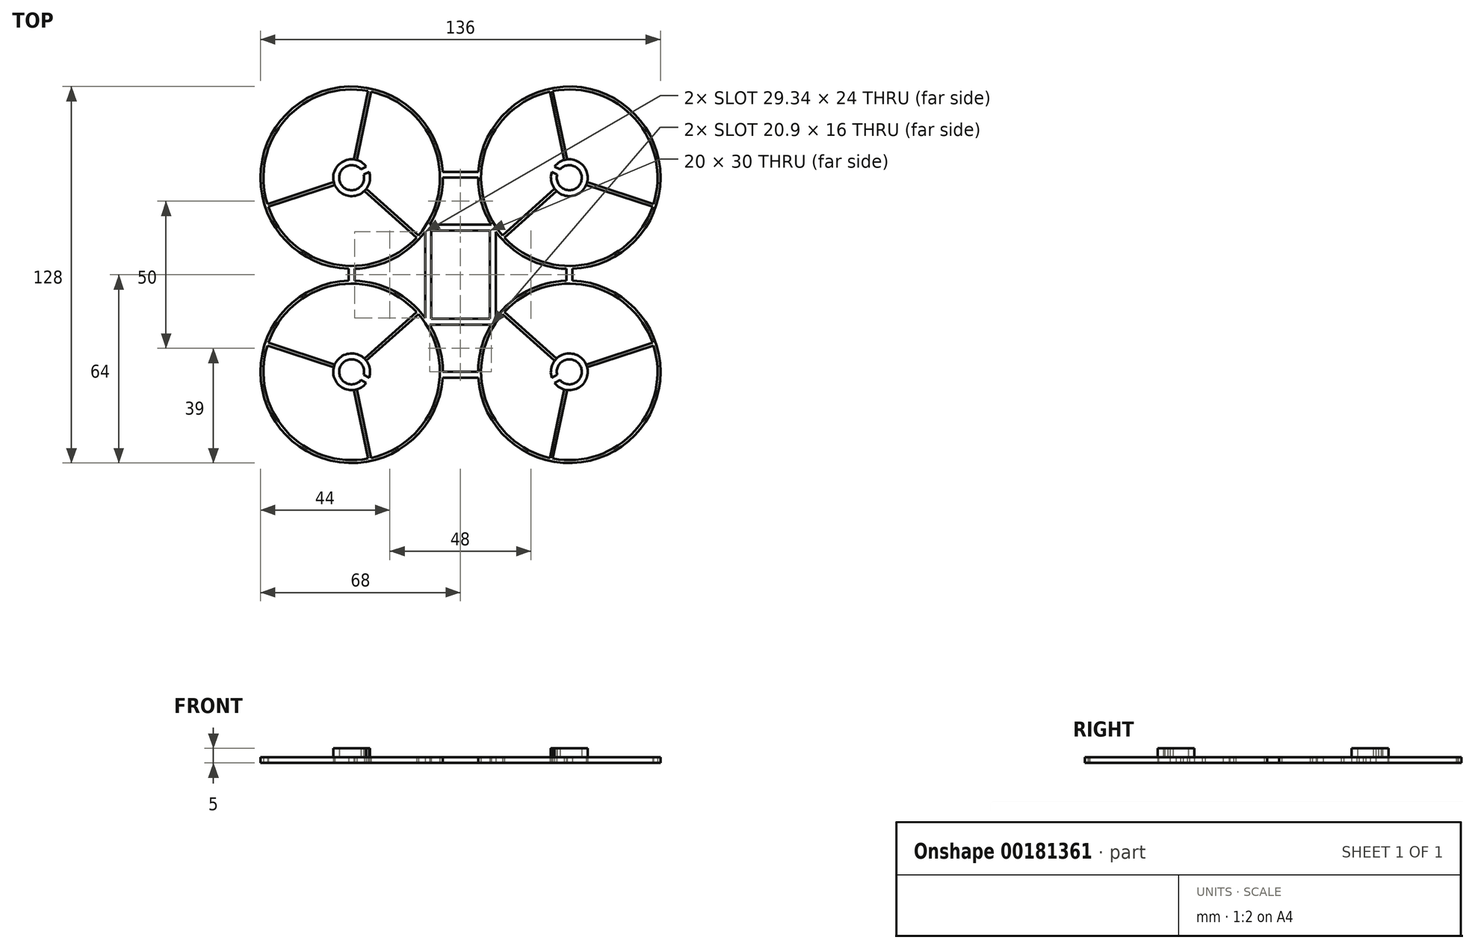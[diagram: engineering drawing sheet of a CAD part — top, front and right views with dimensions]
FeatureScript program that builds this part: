
annotation { "Feature Type Name" : "Feature", "Feature Type Description" : "" }
export const myFeature = defineFeature(function(context is Context, id is Id, definition is map)
    precondition{}
    {
        {
            var Q0;
            Q0=qCreatedBy(makeId("Top.planeOp"),FACE);
            var sketch = newSketch(context, id + "F0", { "sketchPlane" : qUnion([Q0])});
            skLineSegment(sketch, "E0.bottom", {"start": v(10, -15) * mm, "end": v(-10, -15) * mm});
            skLineSegment(sketch, "E0.left", {"start": v(10, -15) * mm, "end": v(10, 15) * mm});
            skPoint(sketch, "E0.middle", {"position": v(0, 0) * mm});
            skLineSegment(sketch, "E1.trimOffspring", {"start": v(-10, -15) * mm, "end": v(-10, 15) * mm});
            skPoint(sketch, "E0.right.start.orphan", {"position": v(-10, -15) * mm});
            skPoint(sketch, "E2.orphan", {"position": v(10, -15) * mm});
            skLineSegment(sketch, "E3.trimOffspring", {"start": v(10, 15) * mm, "end": v(-10, 15) * mm});
            skPoint(sketch, "E0.top.start.orphan", {"position": v(10, 15) * mm});
            skPoint(sketch, "E4.trimOffspring.end.orphan", {"position": v(-10, 15) * mm});
            skLineSegment(sketch, "E5", {"start": v(0, 0) * mm, "end": v(-37, 0) * mm});
            skCircle(sketch, "E6", {"center": v(-37, 33) * mm, "radius": 30 * mm});
            skCircle(sketch, "E7", {"center": v(-37, -33) * mm, "radius": 30 * mm});
            skArc(sketch, "E8", {"start": v(-10.45, 17) * mm, "mid": v(-7.13, 24.7) * mm, "end": v(-6, 33) * mm});
            skArc(sketch, "E9", {"start": v(-12, -14.67) * mm, "mid": v(-22.54, -5.58) * mm, "end": v(-36, -2.02) * mm});
            skLineSegment(sketch, "E10.0", {"start": v(-12, -14.67) * mm, "end": v(-12, 14.67) * mm});
            skLineSegment(sketch, "E11.0", {"start": v(10.45, 17) * mm, "end": v(-10.45, 17) * mm});
            skLineSegment(sketch, "E12.0", {"start": v(12, -14.67) * mm, "end": v(12, 14.67) * mm});
            skLineSegment(sketch, "E13.0", {"start": v(10.45, -17) * mm, "end": v(-10.45, -17) * mm});
            skCircle(sketch, "E14.MirrorC", {"center": v(37, -33) * mm, "radius": 30 * mm});
            skArc(sketch, "E15.MirrorC", {"start": v(10.45, 17) * mm, "mid": v(7.13, 24.7) * mm, "end": v(6, 33) * mm});
            skCircle(sketch, "E16.MirrorC", {"center": v(37, 33) * mm, "radius": 30 * mm});
            skArc(sketch, "E17.MirrorC", {"start": v(12, -14.67) * mm, "mid": v(22.54, -5.58) * mm, "end": v(36, -2.02) * mm});
            skLineSegment(sketch, "E18.0", {"start": v(-36, -2.02) * mm, "end": v(-36, 2.02) * mm});
            skLineSegment(sketch, "E19.0", {"start": v(-38, -2.02) * mm, "end": v(-38, 2.02) * mm});
            skArc(sketch, "E20.trimOffspring", {"start": v(-36, 2.02) * mm, "mid": v(-22.54, 5.58) * mm, "end": v(-12, 14.67) * mm});
            skArc(sketch, "E21.trimOffspring", {"start": v(-38, -2.02) * mm, "mid": v(-59.27, -54.56) * mm, "end": v(-6.06, -35) * mm});
            skLineSegment(sketch, "E22", {"start": v(-6, 33) * mm, "end": v(6, 33) * mm});
            skLineSegment(sketch, "E23", {"start": v(-6, -33) * mm, "end": v(6, -33) * mm});
            skLineSegment(sketch, "E24.0", {"start": v(-6.06, 35) * mm, "end": v(6.06, 35) * mm});
            skLineSegment(sketch, "E25.0", {"start": v(-6.06, -35) * mm, "end": v(6.06, -35) * mm});
            skArc(sketch, "E26.trimOffspring", {"start": v(-6.06, 35) * mm, "mid": v(-59.27, 54.56) * mm, "end": v(-38, 2.02) * mm});
            skArc(sketch, "E27.trimOffspring", {"start": v(6.06, 35) * mm, "mid": v(59.27, 54.56) * mm, "end": v(38, 2.02) * mm});
            skArc(sketch, "E28.trimOffspring", {"start": v(-6, -33) * mm, "mid": v(-7.13, -24.7) * mm, "end": v(-10.45, -17) * mm});
            skArc(sketch, "E29.trimOffspring", {"start": v(6, -33) * mm, "mid": v(7.13, -24.7) * mm, "end": v(10.45, -17) * mm});
            skLineSegment(sketch, "E30.MirrorCS", {"start": v(36, -2.02) * mm, "end": v(36, 2.02) * mm});
            skLineSegment(sketch, "E31.MirrorCS", {"start": v(38, -2.02) * mm, "end": v(38, 2.02) * mm});
            skArc(sketch, "E32.trimOffspring", {"start": v(36, 2.02) * mm, "mid": v(22.54, 5.58) * mm, "end": v(12, 14.67) * mm});
            skArc(sketch, "E33.trimOffspring", {"start": v(38, -2.02) * mm, "mid": v(59.27, -54.56) * mm, "end": v(6.06, -35) * mm});
            skSolve(sketch);
        }
        {
            var Q0;
            Q0=makeQuery(id+"F0.imprint","IMPRINT",FACE,{"disambiguationData":[TD([[makeQuery(id+"F0.imprint","IMPRINT",EDGE,{"derivedFrom":sQuery(id+"F0.wireOp",EDGE,"E0.bottom")}),1.0]])]});
            extrude(context, id + "F1", {"entities" : qUnion([Q0]), "depth" : 2 * mm});
        }
        {
            var Q0;
            Q0=qCreatedBy(makeId("Top.planeOp"),FACE);
            var sketch = newSketch(context, id + "F2", { "sketchPlane" : qUnion([Q0])});
            skPoint(sketch, "E34.0", {"position": v(-37, 33) * mm});
            skPoint(sketch, "E34.1", {"position": v(-37, -33) * mm});
            skPoint(sketch, "E34.2", {"position": v(37, -33) * mm});
            skPoint(sketch, "E34.3", {"position": v(37, 33) * mm});
            skArc(sketch, "E35", {"start": v(-33.81, 35.81) * mm, "mid": v(-40.76, 31.02) * mm, "end": v(-32.88, 34.04) * mm});
            skArc(sketch, "E36", {"start": v(-32.01, 36.76) * mm, "mid": v(-42.53, 30.08) * mm, "end": v(-31.08, 35) * mm});
            skArc(sketch, "E37.0", {"start": v(-30.41, 62.27) * mm, "mid": v(-30.9, 62.37) * mm, "end": v(-31.4, 62.47) * mm});
            skLineSegment(sketch, "E38.0", {"start": v(-37.16, 33.47) * mm, "end": v(-37.43, 33.38) * mm});
            skLineSegment(sketch, "E39.0", {"start": v(-36.84, 32.53) * mm, "end": v(-37.12, 32.43) * mm});
            skLineSegment(sketch, "E40.0", {"start": v(-36.51, 32.9) * mm, "end": v(-36.45, 33.18) * mm});
            skLineSegment(sketch, "E41.0", {"start": v(-37.49, 33.1) * mm, "end": v(-37.43, 33.38) * mm});
            skLineSegment(sketch, "E42.0", {"start": v(-37.33, 32.63) * mm, "end": v(-37.12, 32.43) * mm});
            skLineSegment(sketch, "E43.0", {"start": v(-36.67, 33.37) * mm, "end": v(-36.45, 33.18) * mm});
            skLineSegment(sketch, "E44.trimOffspring", {"start": v(-35.24, 39) * mm, "end": v(-30.41, 62.27) * mm});
            skLineSegment(sketch, "E45.trimOffspring", {"start": v(-36.22, 39.2) * mm, "end": v(-31.4, 62.48) * mm});
            skLineSegment(sketch, "E46.trimOffspring", {"start": v(-32.02, 29.23) * mm, "end": v(-14.28, 13.4) * mm});
            skLineSegment(sketch, "E47.trimOffspring", {"start": v(-32.68, 28.48) * mm, "end": v(-14.95, 12.66) * mm});
            skLineSegment(sketch, "E48.trimOffspring", {"start": v(-42.76, 30.57) * mm, "end": v(-65.33, 23.12) * mm});
            skLineSegment(sketch, "E49.trimOffspring", {"start": v(-43.07, 31.52) * mm, "end": v(-65.64, 24.07) * mm});
            skArc(sketch, "E50.trimOffspring", {"start": v(-14.95, 12.66) * mm, "mid": v(-14.61, 13.03) * mm, "end": v(-14.28, 13.4) * mm});
            skArc(sketch, "E51.trimOffspring", {"start": v(-65.64, 24.07) * mm, "mid": v(-65.49, 23.6) * mm, "end": v(-65.33, 23.12) * mm});
            skLineSegment(sketch, "E52", {"start": v(-37, 33) * mm, "end": v(-36.53, 33.25) * mm});
            skLineSegment(sketch, "E53.0", {"start": v(-32.88, 34.04) * mm, "end": v(-31.08, 35) * mm});
            skLineSegment(sketch, "E54.0", {"start": v(-33.81, 35.81) * mm, "end": v(-32.01, 36.76) * mm});
            skLineSegment(sketch, "E55.MirrorCS", {"start": v(37.16, 33.47) * mm, "end": v(37.43, 33.38) * mm});
            skLineSegment(sketch, "E56.MirrorCS", {"start": v(36.84, 32.53) * mm, "end": v(37.12, 32.43) * mm});
            skLineSegment(sketch, "E57.MirrorCS", {"start": v(37, 33) * mm, "end": v(36.53, 33.25) * mm});
            skLineSegment(sketch, "E58.MirrorCS", {"start": v(37.49, 33.1) * mm, "end": v(37.43, 33.38) * mm});
            skLineSegment(sketch, "E59.MirrorCS", {"start": v(37.33, 32.63) * mm, "end": v(37.12, 32.43) * mm});
            skLineSegment(sketch, "E60.MirrorCS", {"start": v(36.67, 33.37) * mm, "end": v(36.45, 33.18) * mm});
            skLineSegment(sketch, "E61.MirrorCS", {"start": v(36.51, 32.9) * mm, "end": v(36.45, 33.18) * mm});
            skLineSegment(sketch, "E62.MirrorCS", {"start": v(32.88, 34.04) * mm, "end": v(31.08, 35) * mm});
            skArc(sketch, "E63.MirrorCS", {"start": v(30.41, 62.27) * mm, "mid": v(30.9, 62.37) * mm, "end": v(31.4, 62.47) * mm});
            skArc(sketch, "E64.MirrorCS", {"start": v(65.64, 24.07) * mm, "mid": v(65.49, 23.6) * mm, "end": v(65.33, 23.12) * mm});
            skArc(sketch, "E65.MirrorCS", {"start": v(14.95, 12.66) * mm, "mid": v(14.61, 13.03) * mm, "end": v(14.28, 13.4) * mm});
            skLineSegment(sketch, "E66.MirrorCS", {"start": v(33.81, 35.81) * mm, "end": v(32.01, 36.76) * mm});
            skArc(sketch, "E67.MirrorCS", {"start": v(32.01, 36.76) * mm, "mid": v(42.53, 30.08) * mm, "end": v(31.08, 35) * mm});
            skLineSegment(sketch, "E68.MirrorCS", {"start": v(32.68, 28.48) * mm, "end": v(14.95, 12.66) * mm});
            skLineSegment(sketch, "E69.MirrorCS", {"start": v(32.02, 29.23) * mm, "end": v(14.28, 13.4) * mm});
            skLineSegment(sketch, "E70.MirrorCS", {"start": v(43.07, 31.52) * mm, "end": v(65.64, 24.07) * mm});
            skLineSegment(sketch, "E71.MirrorCS", {"start": v(35.24, 39) * mm, "end": v(30.41, 62.27) * mm});
            skLineSegment(sketch, "E72.MirrorCS", {"start": v(42.76, 30.57) * mm, "end": v(65.33, 23.12) * mm});
            skLineSegment(sketch, "E73.MirrorCS", {"start": v(36.22, 39.2) * mm, "end": v(31.4, 62.48) * mm});
            skArc(sketch, "E74.MirrorCS", {"start": v(33.81, 35.81) * mm, "mid": v(40.76, 31.02) * mm, "end": v(32.88, 34.04) * mm});
            skLineSegment(sketch, "E75.MirrorCS", {"start": v(-37, -33) * mm, "end": v(-36.53, -33.25) * mm});
            skLineSegment(sketch, "E76.MirrorCS", {"start": v(-36.84, -32.53) * mm, "end": v(-37.12, -32.43) * mm});
            skLineSegment(sketch, "E77.MirrorCS", {"start": v(-37.16, -33.47) * mm, "end": v(-37.43, -33.38) * mm});
            skLineSegment(sketch, "E78.MirrorCS", {"start": v(-37.33, -32.63) * mm, "end": v(-37.12, -32.43) * mm});
            skLineSegment(sketch, "E79.MirrorCS", {"start": v(-36.67, -33.37) * mm, "end": v(-36.45, -33.18) * mm});
            skLineSegment(sketch, "E80.MirrorCS", {"start": v(-36.51, -32.9) * mm, "end": v(-36.45, -33.18) * mm});
            skLineSegment(sketch, "E81.MirrorCS", {"start": v(36.67, -33.37) * mm, "end": v(36.45, -33.18) * mm});
            skLineSegment(sketch, "E82.MirrorCS", {"start": v(-37.49, -33.1) * mm, "end": v(-37.43, -33.38) * mm});
            skLineSegment(sketch, "E83.MirrorCS", {"start": v(37.49, -33.1) * mm, "end": v(37.43, -33.38) * mm});
            skLineSegment(sketch, "E84.MirrorCS", {"start": v(37.33, -32.63) * mm, "end": v(37.12, -32.43) * mm});
            skLineSegment(sketch, "E85.MirrorCS", {"start": v(37.16, -33.47) * mm, "end": v(37.43, -33.38) * mm});
            skLineSegment(sketch, "E86.MirrorCS", {"start": v(36.84, -32.53) * mm, "end": v(37.12, -32.43) * mm});
            skLineSegment(sketch, "E87.MirrorCS", {"start": v(37, -33) * mm, "end": v(36.53, -33.25) * mm});
            skLineSegment(sketch, "E88.MirrorCS", {"start": v(36.51, -32.9) * mm, "end": v(36.45, -33.18) * mm});
            skLineSegment(sketch, "E89.MirrorCS", {"start": v(-32.88, -34.04) * mm, "end": v(-31.08, -35) * mm});
            skArc(sketch, "E90.MirrorCS", {"start": v(14.95, -12.66) * mm, "mid": v(14.61, -13.03) * mm, "end": v(14.28, -13.4) * mm});
            skArc(sketch, "E91.MirrorCS", {"start": v(30.41, -62.27) * mm, "mid": v(30.9, -62.37) * mm, "end": v(31.4, -62.47) * mm});
            skArc(sketch, "E92.MirrorCS", {"start": v(65.64, -24.07) * mm, "mid": v(65.49, -23.6) * mm, "end": v(65.33, -23.12) * mm});
            skArc(sketch, "E93.MirrorCS", {"start": v(-14.95, -12.66) * mm, "mid": v(-14.61, -13.03) * mm, "end": v(-14.28, -13.4) * mm});
            skLineSegment(sketch, "E94.MirrorCS", {"start": v(33.81, -35.81) * mm, "end": v(32.01, -36.76) * mm});
            skArc(sketch, "E95.MirrorCS", {"start": v(-65.64, -24.07) * mm, "mid": v(-65.49, -23.6) * mm, "end": v(-65.33, -23.12) * mm});
            skLineSegment(sketch, "E96.MirrorCS", {"start": v(-33.81, -35.81) * mm, "end": v(-32.01, -36.76) * mm});
            skArc(sketch, "E97.MirrorCS", {"start": v(-30.41, -62.27) * mm, "mid": v(-30.9, -62.37) * mm, "end": v(-31.4, -62.47) * mm});
            skLineSegment(sketch, "E98.MirrorCS", {"start": v(32.88, -34.04) * mm, "end": v(31.08, -35) * mm});
            skLineSegment(sketch, "E99.MirrorCS", {"start": v(-42.76, -30.57) * mm, "end": v(-65.33, -23.12) * mm});
            skArc(sketch, "E100.MirrorCS", {"start": v(-32.01, -36.76) * mm, "mid": v(-42.53, -30.08) * mm, "end": v(-31.08, -35) * mm});
            skLineSegment(sketch, "E101.MirrorCS", {"start": v(32.02, -29.23) * mm, "end": v(14.28, -13.4) * mm});
            skLineSegment(sketch, "E102.MirrorCS", {"start": v(32.68, -28.48) * mm, "end": v(14.95, -12.66) * mm});
            skLineSegment(sketch, "E103.MirrorCS", {"start": v(-35.24, -39) * mm, "end": v(-30.41, -62.27) * mm});
            skArc(sketch, "E104.MirrorCS", {"start": v(32.01, -36.76) * mm, "mid": v(42.53, -30.08) * mm, "end": v(31.08, -35) * mm});
            skArc(sketch, "E105.MirrorCS", {"start": v(-33.81, -35.81) * mm, "mid": v(-40.76, -31.02) * mm, "end": v(-32.88, -34.04) * mm});
            skLineSegment(sketch, "E106.MirrorCS", {"start": v(43.07, -31.52) * mm, "end": v(65.64, -24.07) * mm});
            skLineSegment(sketch, "E107.MirrorCS", {"start": v(-36.22, -39.2) * mm, "end": v(-31.4, -62.48) * mm});
            skLineSegment(sketch, "E108.MirrorCS", {"start": v(35.24, -39) * mm, "end": v(30.41, -62.27) * mm});
            skLineSegment(sketch, "E109.MirrorCS", {"start": v(-32.68, -28.48) * mm, "end": v(-14.95, -12.66) * mm});
            skLineSegment(sketch, "E110.MirrorCS", {"start": v(42.76, -30.57) * mm, "end": v(65.33, -23.12) * mm});
            skLineSegment(sketch, "E111.MirrorCS", {"start": v(-43.07, -31.52) * mm, "end": v(-65.64, -24.07) * mm});
            skLineSegment(sketch, "E112.MirrorCS", {"start": v(-32.02, -29.23) * mm, "end": v(-14.28, -13.4) * mm});
            skLineSegment(sketch, "E113.MirrorCS", {"start": v(36.22, -39.2) * mm, "end": v(31.4, -62.48) * mm});
            skArc(sketch, "E114.MirrorCS", {"start": v(33.81, -35.81) * mm, "mid": v(40.76, -31.02) * mm, "end": v(32.88, -34.04) * mm});
            skSolve(sketch);
        }
        {
            var Q0;
            Q0 = qSketchRegion(id + "F2", true);
            extrude(context, id + "F3", {"entities" : qUnion([Q0]), "operationType" : NewBodyOperationType.ADD, "depth" : 2 * mm});
        }
        {
            var Q0;
            Q0=makeQuery(id+"F3.boolean.opBoolean","MERGE",FACE,{"derivedFrom":[makeQuery(id+"F1.opExtrude","CAP_FACE",FACE,{"disambiguationData":[OSD([sQuery(id+"F0.wireOp",EDGE,"E0.bottom"),sQuery(id+"F0.wireOp",EDGE,"E0.left"),sQuery(id+"F0.wireOp",EDGE,"8eY0ywfV-9Z6W-Qo5m-D8jn-J49xxAZvXbwB"),sQuery(id+"F0.wireOp",EDGE,"Xtx9QI3k-f51G-aEG8-mtxL-sKhmU4RuaAeC"),sQuery(id+"F0.wireOp",EDGE,"h6kVLv3e-dve9-XwBx-Bzxx-gdcmmZpf07Xi"),sQuery(id+"F0.wireOp",EDGE,"ZlAXJ9HC-sCrh-7Fj3-LRwR-778SMyBQQJ9o"),sQuery(id+"F0.wireOp",EDGE,"5T0wLuSs-AjmY-yiY1-RF5I-zBbIXbfDyhT2"),sQuery(id+"F0.wireOp",EDGE,"fl3oA5yA-FJmu-GqFl-83ii-te1wL3NXjBQd"),sQuery(id+"F0.wireOp",EDGE,"EaOwJ7Dt-GguA-I4Ys-FBLc-F2PJPnprf8aF"),sQuery(id+"F0.wireOp",EDGE,"ENn3r0Vk-cs1r-paBJ-yqdQ-5ZDpOucUYL6t"),sQuery(id+"F0.wireOp",EDGE,"elssh5FO-xy5j-3K2W-xatG-TW6KUt95clqc"),sQuery(id+"F0.wireOp",EDGE,"hN8ZmCmT-rimr-s7UP-4TKk-hWlfrN4nuHw0"),sQuery(id+"F0.wireOp",EDGE,"VlVE9LhR-VQfP-osfL-6FSO-uC9llmzmiDNa"),sQuery(id+"F0.wireOp",EDGE,"8cPBi7kA-Zb0s-XOpn-rokd-xlJVSZItnVir"),sQuery(id+"F0.wireOp",EDGE,"da322b16-46d2-4a8f-bded-c1b00f84780c.0"),sQuery(id+"F0.wireOp",EDGE,"7d3005c1-0569-4dc9-8728-1ab2c7c93ee6.0"),sQuery(id+"F0.wireOp",EDGE,"ef316d98-2606-48e0-be53-918bc2cb5e0b.0"),sQuery(id+"F0.wireOp",EDGE,"0924762f-375b-4b02-86ac-d213c3efb8b4.0"),sQuery(id+"F0.wireOp",EDGE,"E1.trimOffspring"),sQuery(id+"F0.wireOp",EDGE,"9dcf11ad-c5b0-445f-ad27-298aeb594cdf.trimOffspring"),sQuery(id+"F0.wireOp",EDGE,"cee0878e-4c5d-4474-aa39-deb348d99536.trimOffspring"),sQuery(id+"F0.wireOp",EDGE,"2700a6e3-2a09-44ea-8bac-d7e64ac7073c.trimOffspring"),sQuery(id+"F0.wireOp",EDGE,"668b03c5-ca19-42fb-8b17-b9e992777853.trimOffspring"),sQuery(id+"F0.wireOp",EDGE,"5badcddb-8162-4ce3-ad40-95f5f7c46b8e.trimOffspring"),sQuery(id+"F0.wireOp",EDGE,"2c8a510c-2891-4925-a239-b100359e3c29.trimOffspring"),sQuery(id+"F0.wireOp",EDGE,"290c4de5-aa1b-4537-96c7-af5b9a8db3a0.trimOffspring"),sQuery(id+"F0.wireOp",EDGE,"abed33b1-e551-43fb-a86a-55be2662da60.trimOffspring"),sQuery(id+"F0.wireOp",EDGE,"E3.trimOffspring"),sQuery(id+"F0.wireOp",EDGE,"84992064-a970-43a4-b508-db4936c2debd.0"),sQuery(id+"F0.wireOp",EDGE,"8db73eb8-7cd4-4fdf-8231-31e9e81fec03.0"),sQuery(id+"F0.wireOp",EDGE,"188f87f6-274d-4501-a73e-5f412ec5c7be.0"),sQuery(id+"F0.wireOp",EDGE,"a69325de-3d90-4af7-bf6d-652e6c802c99.0"),sQuery(id+"F0.wireOp",EDGE,"kjFVXY6S-cpiz-Y1Cz-QEHZ-oqtZtCCTOBGc"),sQuery(id+"F0.wireOp",EDGE,"7sG6gPkX-hC2C-EOb8-0SL6-mwDeZgZtWL4g"),sQuery(id+"F0.wireOp",EDGE,"zuwm9blg-SwqF-LY98-IXgh-TO7BUMBQW6x9"),sQuery(id+"F0.wireOp",EDGE,"dV4IKqJ1-oU1c-nKPh-nYmV-SWWtcWYGKtiM")])],"isStart":false}),makeQuery(id+"F3.opExtrude","CAP_FACE",FACE,{"disambiguationData":[OSD([sQuery(id+"F2.wireOp",EDGE,"84KwVwdS-LAR0-l09K-39Wu-ycXSRmMj6il8"),sQuery(id+"F2.wireOp",EDGE,"3tuRaFak-gwi4-yJU6-Vqaf-7BudujC2kCUT"),sQuery(id+"F2.wireOp",EDGE,"56dd305f-a435-46cf-a3d2-c01ebf28b73c.trimOffspring"),sQuery(id+"F2.wireOp",EDGE,"cb30fa8a-5316-4f5f-ab30-ca89d61c2ddd.trimOffspring"),sQuery(id+"F2.wireOp",EDGE,"b2c1d309-7a88-4eb5-b876-e4ba8b21249d.trimOffspring"),sQuery(id+"F2.wireOp",EDGE,"0473c5be-f102-4da5-941d-497e3bbcbe9e.trimOffspring"),sQuery(id+"F2.wireOp",EDGE,"ee1f42fc-6ba4-4799-a05a-f82ee215a58e.trimOffspring"),sQuery(id+"F2.wireOp",EDGE,"f4be61ec-9dac-4f06-94ab-087b2e39aaa0.trimOffspring"),sQuery(id+"F2.wireOp",EDGE,"4ff711a9-feef-4413-9574-0342b69596f0.trimOffspring"),sQuery(id+"F2.wireOp",EDGE,"98585caf-8288-423b-bc6f-ab68b5ebcf4b.trimOffspring"),sQuery(id+"F2.wireOp",EDGE,"eedd28db-2f91-460a-ae4c-cb2ba9cc7f77.trimOffspring"),sQuery(id+"F2.wireOp",EDGE,"f043c2df-18cc-427e-9854-83e3c715cedc.trimOffspring"),sQuery(id+"F2.wireOp",EDGE,"WjcNrnuk-0Vk4-qrJK-7t3g-P4dkHSyzrQl7"),sQuery(id+"F2.wireOp",EDGE,"142e0f77-5f94-4a1f-be21-3b73fc2f5bad.32"),sQuery(id+"F2.wireOp",EDGE,"c9cd9590-805b-4d9d-a0b4-2a0f59433488.trimOffspring"),sQuery(id+"F2.wireOp",EDGE,"b18628f9-f9ee-4cd6-8a71-322e16da2bd3.trimOffspring")])],"isStart":false}),makeQuery(id+"F3.opExtrude","CAP_FACE",FACE,{"disambiguationData":[OSD([sQuery(id+"F2.wireOp",EDGE,"18cfd82f-b097-47b0-a57a-080757fb61528.MirrorCS"),sQuery(id+"F2.wireOp",EDGE,"18cfd82f-b097-47b0-a57a-080757fb61529.MirrorCS"),sQuery(id+"F2.wireOp",EDGE,"18cfd82f-b097-47b0-a57a-080757fb615210.MirrorCS"),sQuery(id+"F2.wireOp",EDGE,"18cfd82f-b097-47b0-a57a-080757fb615212.MirrorCS"),sQuery(id+"F2.wireOp",EDGE,"18cfd82f-b097-47b0-a57a-080757fb615215.MirrorCS"),sQuery(id+"F2.wireOp",EDGE,"18cfd82f-b097-47b0-a57a-080757fb615216.MirrorCS"),sQuery(id+"F2.wireOp",EDGE,"18cfd82f-b097-47b0-a57a-080757fb615217.MirrorCS"),sQuery(id+"F2.wireOp",EDGE,"18cfd82f-b097-47b0-a57a-080757fb615218.MirrorCS"),sQuery(id+"F2.wireOp",EDGE,"18cfd82f-b097-47b0-a57a-080757fb615219.MirrorCS"),sQuery(id+"F2.wireOp",EDGE,"18cfd82f-b097-47b0-a57a-080757fb615220.MirrorCS"),sQuery(id+"F2.wireOp",EDGE,"18cfd82f-b097-47b0-a57a-080757fb615221.MirrorCS"),sQuery(id+"F2.wireOp",EDGE,"18cfd82f-b097-47b0-a57a-080757fb615222.MirrorCS"),sQuery(id+"F2.wireOp",EDGE,"18cfd82f-b097-47b0-a57a-080757fb615223.MirrorCS"),sQuery(id+"F2.wireOp",EDGE,"95046510-c853-408b-81f3-02322cb645c1.0"),sQuery(id+"F2.wireOp",EDGE,"abb661df-539f-4126-b30a-783ae723f974.trimOffspring"),sQuery(id+"F2.wireOp",EDGE,"be1bb378-8a4b-4d11-a47e-b5b4169adf51.trimOffspring")])],"isStart":false}),makeQuery(id+"F3.opExtrude","CAP_FACE",FACE,{"disambiguationData":[OSD([sQuery(id+"F2.wireOp",EDGE,"4b403e7a-ee7c-4a93-a97b-abf5346f50b016.MirrorCS"),sQuery(id+"F2.wireOp",EDGE,"4b403e7a-ee7c-4a93-a97b-abf5346f50b017.MirrorCS"),sQuery(id+"F2.wireOp",EDGE,"4b403e7a-ee7c-4a93-a97b-abf5346f50b018.MirrorCS"),sQuery(id+"F2.wireOp",EDGE,"4b403e7a-ee7c-4a93-a97b-abf5346f50b022.MirrorCS"),sQuery(id+"F2.wireOp",EDGE,"4b403e7a-ee7c-4a93-a97b-abf5346f50b030.MirrorCS"),sQuery(id+"F2.wireOp",EDGE,"4b403e7a-ee7c-4a93-a97b-abf5346f50b034.MirrorCS"),sQuery(id+"F2.wireOp",EDGE,"4b403e7a-ee7c-4a93-a97b-abf5346f50b035.MirrorCS"),sQuery(id+"F2.wireOp",EDGE,"4b403e7a-ee7c-4a93-a97b-abf5346f50b036.MirrorCS"),sQuery(id+"F2.wireOp",EDGE,"4b403e7a-ee7c-4a93-a97b-abf5346f50b037.MirrorCS"),sQuery(id+"F2.wireOp",EDGE,"4b403e7a-ee7c-4a93-a97b-abf5346f50b042.MirrorCS"),sQuery(id+"F2.wireOp",EDGE,"4b403e7a-ee7c-4a93-a97b-abf5346f50b044.MirrorCS"),sQuery(id+"F2.wireOp",EDGE,"4b403e7a-ee7c-4a93-a97b-abf5346f50b045.MirrorCS"),sQuery(id+"F2.wireOp",EDGE,"4b403e7a-ee7c-4a93-a97b-abf5346f50b047.MirrorCS"),sQuery(id+"F2.wireOp",EDGE,"34ac5828-68e1-45c2-aa1b-1277871d3fcc.0"),sQuery(id+"F2.wireOp",EDGE,"85acdcf5-a78e-47d3-a57e-60c025f3261f.trimOffspring"),sQuery(id+"F2.wireOp",EDGE,"e868a208-1e75-41d9-91cc-819774f794d4.trimOffspring")])],"isStart":false}),makeQuery(id+"F3.opExtrude","CAP_FACE",FACE,{"disambiguationData":[OSD([sQuery(id+"F2.wireOp",EDGE,"4b403e7a-ee7c-4a93-a97b-abf5346f50b020.MirrorCS"),sQuery(id+"F2.wireOp",EDGE,"4b403e7a-ee7c-4a93-a97b-abf5346f50b021.MirrorCS"),sQuery(id+"F2.wireOp",EDGE,"4b403e7a-ee7c-4a93-a97b-abf5346f50b023.MirrorCS"),sQuery(id+"F2.wireOp",EDGE,"4b403e7a-ee7c-4a93-a97b-abf5346f50b025.MirrorCS"),sQuery(id+"F2.wireOp",EDGE,"4b403e7a-ee7c-4a93-a97b-abf5346f50b026.MirrorCS"),sQuery(id+"F2.wireOp",EDGE,"4b403e7a-ee7c-4a93-a97b-abf5346f50b028.MirrorCS"),sQuery(id+"F2.wireOp",EDGE,"4b403e7a-ee7c-4a93-a97b-abf5346f50b029.MirrorCS"),sQuery(id+"F2.wireOp",EDGE,"4b403e7a-ee7c-4a93-a97b-abf5346f50b031.MirrorCS"),sQuery(id+"F2.wireOp",EDGE,"4b403e7a-ee7c-4a93-a97b-abf5346f50b032.MirrorCS"),sQuery(id+"F2.wireOp",EDGE,"4b403e7a-ee7c-4a93-a97b-abf5346f50b033.MirrorCS"),sQuery(id+"F2.wireOp",EDGE,"4b403e7a-ee7c-4a93-a97b-abf5346f50b038.MirrorCS"),sQuery(id+"F2.wireOp",EDGE,"4b403e7a-ee7c-4a93-a97b-abf5346f50b039.MirrorCS"),sQuery(id+"F2.wireOp",EDGE,"4b403e7a-ee7c-4a93-a97b-abf5346f50b040.MirrorCS"),sQuery(id+"F2.wireOp",EDGE,"4b403e7a-ee7c-4a93-a97b-abf5346f50b041.MirrorCS"),sQuery(id+"F2.wireOp",EDGE,"4b403e7a-ee7c-4a93-a97b-abf5346f50b043.MirrorCS"),sQuery(id+"F2.wireOp",EDGE,"4b403e7a-ee7c-4a93-a97b-abf5346f50b046.MirrorCS")])],"isStart":false})]});
            var sketch = newSketch(context, id + "F4", { "sketchPlane" : qUnion([Q0])});
            skArc(sketch, "E115.0", {"start": v(-33.81, 35.81) * mm, "mid": v(-40.76, 31.02) * mm, "end": v(-32.88, 34.04) * mm});
            skLineSegment(sketch, "E115.1", {"start": v(-33.81, 35.81) * mm, "end": v(-32.01, 36.76) * mm});
            skLineSegment(sketch, "E115.2", {"start": v(-32.88, 34.04) * mm, "end": v(-31.08, 35) * mm});
            skArc(sketch, "E116", {"start": v(-32.01, 36.76) * mm, "mid": v(-42.53, 30.08) * mm, "end": v(-31.08, 35) * mm});
            skLineSegment(sketch, "E117.MirrorCS", {"start": v(32.88, 34.04) * mm, "end": v(31.08, 35) * mm});
            skLineSegment(sketch, "E118.MirrorCS", {"start": v(33.81, 35.81) * mm, "end": v(32.01, 36.76) * mm});
            skArc(sketch, "E119.MirrorCS", {"start": v(33.81, 35.81) * mm, "mid": v(40.76, 31.02) * mm, "end": v(32.88, 34.04) * mm});
            skArc(sketch, "E120.MirrorCS", {"start": v(32.01, 36.76) * mm, "mid": v(42.53, 30.08) * mm, "end": v(31.08, 35) * mm});
            skLineSegment(sketch, "E121.MirrorCS", {"start": v(32.88, -34.04) * mm, "end": v(31.08, -35) * mm});
            skLineSegment(sketch, "E122.MirrorCS", {"start": v(-33.81, -35.81) * mm, "end": v(-32.01, -36.76) * mm});
            skLineSegment(sketch, "E123.MirrorCS", {"start": v(-32.88, -34.04) * mm, "end": v(-31.08, -35) * mm});
            skLineSegment(sketch, "E124.MirrorCS", {"start": v(33.81, -35.81) * mm, "end": v(32.01, -36.76) * mm});
            skArc(sketch, "E125.MirrorCS", {"start": v(-32.01, -36.76) * mm, "mid": v(-42.53, -30.08) * mm, "end": v(-31.08, -35) * mm});
            skArc(sketch, "E126.MirrorCS", {"start": v(33.81, -35.81) * mm, "mid": v(40.76, -31.02) * mm, "end": v(32.88, -34.04) * mm});
            skArc(sketch, "E127.MirrorCS", {"start": v(-33.81, -35.81) * mm, "mid": v(-40.76, -31.02) * mm, "end": v(-32.88, -34.04) * mm});
            skArc(sketch, "E128.MirrorCS", {"start": v(32.01, -36.76) * mm, "mid": v(42.53, -30.08) * mm, "end": v(31.08, -35) * mm});
            skSolve(sketch);
        }
        {
            var Q0;
            Q0=makeQuery(id+"F4.imprint","IMPRINT",FACE,{"disambiguationData":[TD([[makeQuery(id+"F4.imprint","IMPRINT",EDGE,{"derivedFrom":sQuery(id+"F4.wireOp",EDGE,"E115.0")}),-1.0]])]});
            var Q1;
            {var subQ6=sQuery(id+"F4.wireOp",EDGE,"E117.MirrorCS");Q1=makeQuery(id+"F4.imprint","IMPRINT",FACE,{"disambiguationData":[TD([[makeQuery(id+"F4.imprint","IMPRINT",EDGE,{"derivedFrom":subQ6}),1.0]])]});}
            var Q2;
            {var subQ5=sQuery(id+"F4.wireOp",EDGE,"E122.MirrorCS");Q2=makeQuery(id+"F4.imprint","IMPRINT",FACE,{"disambiguationData":[TD([[makeQuery(id+"F4.imprint","IMPRINT",EDGE,{"derivedFrom":subQ5}),-1.0]])]});}
            var Q3;
            {var subQ7=sQuery(id+"F4.wireOp",EDGE,"E121.MirrorCS");Q3=makeQuery(id+"F4.imprint","IMPRINT",FACE,{"disambiguationData":[TD([[makeQuery(id+"F4.imprint","IMPRINT",EDGE,{"derivedFrom":subQ7}),-1.0]])]});}
            extrude(context, id + "F5", {"entities" : qUnion([Q0, Q1, Q2, Q3]), "operationType" : NewBodyOperationType.ADD, "depth" : 3 * mm});
        }
    });
